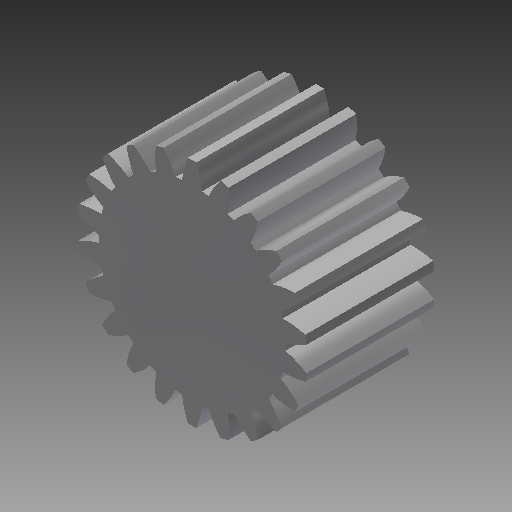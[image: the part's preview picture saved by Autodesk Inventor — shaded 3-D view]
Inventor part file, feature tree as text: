
AUTODESK INVENTOR PART (.ipt)
format: ipt  version: 2019 (Build 230136000, 136)  size: 239,616 bytes
history: native  units: mm (DEFAULTED — no unit token found)
features: plane x3, other x3, sketch x2, extrude x1
ambient origin geometry x8: Origin, YZ Plane, XZ Plane, XY Plane, X Axis, Y Axis, Z Axis, Center Point
bodies: Solid1 (feature_tree)
feature tree (9):
  extrude  "Extrusion1"  Depth=20.0mm TaperAngle=0.0deg
  plane  "Work Plane2"
  plane  "Work Plane8"
  plane  "Work Plane9"
  other  "正齒輪"
  sketch  "Sketch1"  dims[d0=36.0mm d1=20.0mm d2=0.0mm]
  sketch  "Sketch2"  dims[d3=31.538296mm d4=10.0mm d5=0.0mm d16=9.318133mm d17=0.0mm d34=1.427997mm d39=0.0mm d41=0.0mm d43=9.318133mm d46=9.318133mm d47=0.0mm d48=0.0mm]
  other  "Srf1"
  other  "節圓直徑"
